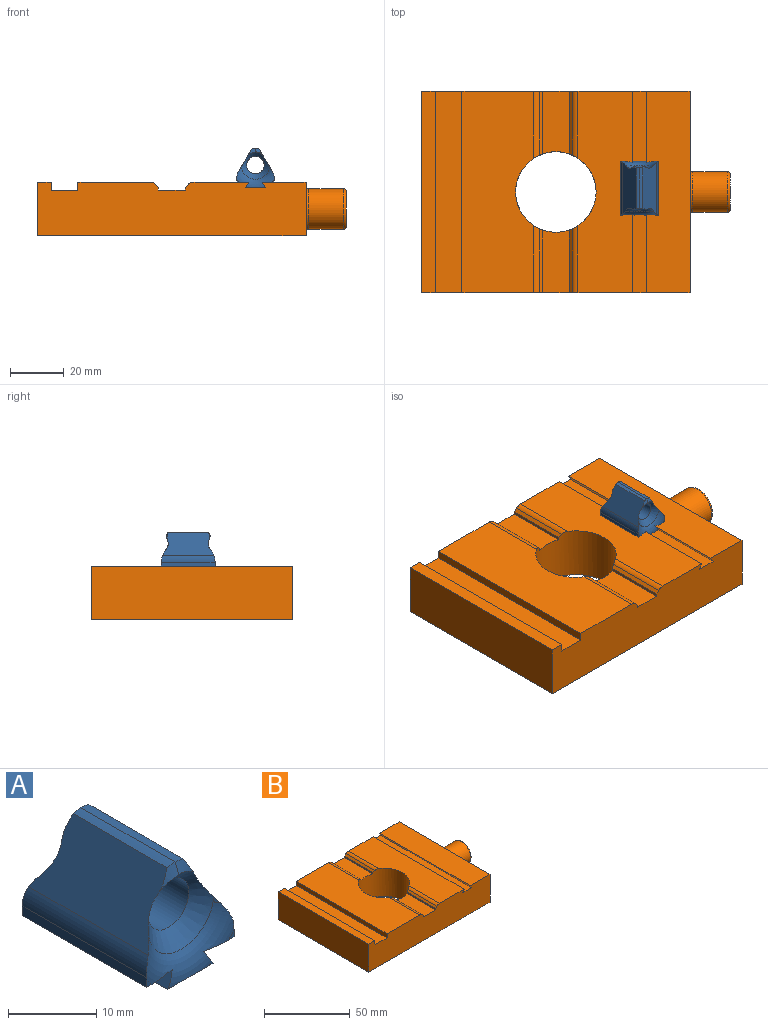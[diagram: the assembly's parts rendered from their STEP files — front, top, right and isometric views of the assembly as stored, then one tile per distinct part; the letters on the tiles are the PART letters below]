
ASSEMBLY  parts=2 mates=1
PART A: 30 faces, bbox 28.4x21.8x21.6 mm
  f0: plane 0.99x0.88mm, normal (0,1,0), area 0.4mm2, adj f6,f12,f29
  f1: plane 0.72x0.23mm, normal (0,1,0), area 0.1mm2, adj f7,f8,f29
  f2: plane 0.75x0.24mm, normal (0,1,0), area 0.1mm2, adj f8,f9,f29
  f3: plane 0.99x0.88mm, normal (0,-1,0), area 0.4mm2, adj f10,f11,f28
  f4: plane 0.75x0.24mm, normal (0,-1,0), area 0.1mm2, adj f8,f9,f28
  f5: plane 0.72x0.23mm, normal (0,-1,0), area 0.1mm2, adj f7,f8,f28
  f6: plane 20x4.54mm, normal (0,0,-1), area 89.6mm2, adj f0,f7,f12,f13,f28,f29
  f7: plane 20.03x2.02mm, normal (-0.87,0,0.5), area 45.4mm2, adj f1,f5,f6,f8,f28,f29
  f8: plane 20x7.3mm, normal (0,0,-1), area 145.8mm2, adj f1,f2,f4,f5,f7,f9,f28,f29
  f9: plane 20.03x2.02mm, normal (0.87,0,0.5), area 45.4mm2, adj f2,f4,f8,f10,f28,f29
  f10: plane 20x4.51mm, normal (0,0,-1), area 89mm2, adj f3,f9,f11,f14,f28,f29
  f11: plane 20x1.35mm, normal (1,0,0), area 26.9mm2, adj f3,f10,f14,f20,f28,f29
  f12: plane 20x1.35mm, normal (-1,0,0), area 26.9mm2, adj f0,f6,f13,f21,f28,f29
  f13: plane 0.99x0.88mm, normal (0,-1,0), area 0.4mm2, adj f6,f12,f28
  f14: plane 0.99x0.88mm, normal (0,1,0), area 0.4mm2, adj f10,f11,f29
  f15: cylinder r=3.27mm len=13mm, axis (0,-1,0), area 266.7mm2, adj f22,f23
  f16: cylinder r=5mm len=15.17mm, axis (0,-1,0), area 19.4mm2, adj f17,f19,f25,f27
  f17: cylinder r=5mm len=15.17mm, axis (0,-1,0), area 19.4mm2, adj f16,f18,f24,f26
  f18: plane 20.95x10.46mm, normal (0.86,0,0.51), area 161.1mm2, adj f17,f20,f22,f23,f24,f26,f28,f29
  f19: plane 20.95x10.47mm, normal (-0.86,0,0.51), area 161.1mm2, adj f16,f21,f22,f23,f25,f27,f28,f29
  f20: cylinder r=5mm len=19.99mm, axis (0,-1,0), area 51.8mm2, adj f11,f18,f28,f29
  f21: cylinder r=5mm len=19.99mm, axis (0,-1,0), area 51.8mm2, adj f12,f19,f28,f29
  f22: cone r=3.27mm half-angle=45deg, axis (0,-1,0), area 66.3mm2, adj f15,f18,f19,f24,f25,f28
  f23: cone r=6.77mm half-angle=45deg, axis (0,1,0), area 66.2mm2, adj f15,f18,f19,f26,f27,f29
  f24: bspline ~3.83x2.81mm, area 3.7mm2, adj f17,f18,f22,f25
  f25: bspline ~3.82x2.81mm, area 3.7mm2, adj f16,f19,f22,f24
  f26: bspline ~4.22x3.06mm, area 3.7mm2, adj f17,f18,f23,f27
  f27: bspline ~4.23x3.06mm, area 3.7mm2, adj f16,f19,f23,f26
  f28: torus R=8.84mm, axis (0,-1,0), area 54.5mm2, adj f3,f4,f5,f6,f7,f8,f9,f10
  f29: torus R=8.84mm, axis (0,-1,0), area 54.5mm2, adj f0,f1,f2,f6,f7,f8,f9,f10
PART B: 34 faces, bbox 115x75x20 mm
  f0: plane 75x16.35mm, normal (0,0,1), area 1225.9mm2, adj f1,f5,f6,f20
  f1: plane 100x20mm, normal (0,-1,0), area 1923.3mm2, adj f0,f3,f4,f5,f7,f8,f9,f10
  f2: cylinder r=15mm len=30mm, axis (0,0,-1), area 1814.2mm2, adj f3,f4,f9,f10,f11,f12,f13,f14
  f3: plane 75x26.76mm, normal (0,0,1), area 1887.6mm2, adj f1,f2,f6,f16,f32,f33
  f4: plane 75x20.41mm, normal (0,0,1), area 1411.7mm2, adj f1,f2,f6,f21,f30,f31
  f5: plane 75x20mm, normal (1,0,0), area 1273mm2, adj f0,f1,f6,f9,f24
  f6: plane 100x20mm, normal (0,1,0), area 1923.3mm2, adj f0,f3,f4,f5,f7,f8,f9,f13
  f7: plane 75x20mm, normal (-1,0,0), area 1500mm2, adj f1,f6,f8,f9
  f8: plane 75x5mm, normal (0,0,1), area 375mm2, adj f1,f6,f7,f17
  f9: plane 100x75mm, normal (0,0,-1), area 6793.1mm2, adj f1,f2,f5,f6,f7
  f10: plane 23.36x1mm, normal (-1,0,0), area 23.4mm2, adj f1,f2,f12,f28
  f11: plane 23.36x1mm, normal (1,0,0), area 23.4mm2, adj f1,f2,f12,f27
  f12: plane 23.36x10mm, normal (0,0,1), area 227.8mm2, adj f1,f2,f10,f11
  f13: plane 23.36x1mm, normal (-1,0,0), area 23.4mm2, adj f2,f6,f15,f29
  f14: plane 23.36x1mm, normal (1,0,0), area 23.4mm2, adj f2,f6,f15,f26
  f15: plane 23.36x10mm, normal (0,0,1), area 227.8mm2, adj f2,f6,f13,f14
  f16: plane 75x3mm, normal (-1,0,0), area 225mm2, adj f1,f3,f6,f18
  f17: plane 75x3mm, normal (1,0,0), area 225mm2, adj f1,f6,f8,f18
  f18: plane 75x10mm, normal (0,0,1), area 750mm2, adj f1,f6,f16,f17
  f19: plane 75x7.31mm, normal (0,0,1), area 548.2mm2, adj f1,f6,f20,f21
  f20: plane 75x2mm, normal (-0.87,0,-0.5), area 173.2mm2, adj f0,f1,f6,f19
  f21: plane 75x2mm, normal (0.87,0,-0.5), area 173.2mm2, adj f1,f4,f6,f19
  f22: cylinder r=7.5mm len=15mm, axis (-1,0,0), area 612.6mm2, adj f24,f25
  f23: plane 13x13mm, normal (1,0,0), area 132.7mm2, adj f25
  f24: torus R=8.5mm, axis (1,0,0), area 77.6mm2, adj f5,f22
  f25: torus R=6.5mm, axis (1,0,0), area 70.4mm2, adj f22,f23
  f26: plane 23.81x1.13mm, normal (0.71,0,0.71), area 37.4mm2, adj f2,f6,f14,f32
  f27: plane 23.81x1.13mm, normal (0.71,0,0.71), area 37.4mm2, adj f1,f2,f11,f33
  f28: plane 23.81x1.13mm, normal (-0.71,0,0.71), area 37.4mm2, adj f1,f2,f10,f30
  f29: plane 23.81x1.13mm, normal (-0.71,0,0.71), area 37.4mm2, adj f2,f6,f13,f31
  f30: cylinder r=3mm len=24.97mm, axis (0,-1,0), area 57.3mm2, adj f1,f2,f4,f28
  f31: cylinder r=3mm len=24.97mm, axis (0,-1,0), area 57.3mm2, adj f2,f4,f6,f29
  f32: cylinder r=3mm len=24.97mm, axis (0,1,0), area 57.3mm2, adj f2,f3,f6,f26
  f33: cylinder r=3mm len=24.97mm, axis (0,1,0), area 57.3mm2, adj f1,f2,f3,f27
PLACE A t=(25.84,23.64,47.39)mm
PLACE B t=(-7.82,12.24,0.66)mm fixed
MATE slider A.f2 <-> B.f6  axis (0,1,0) through (26.99,23.64,18.66)mm
